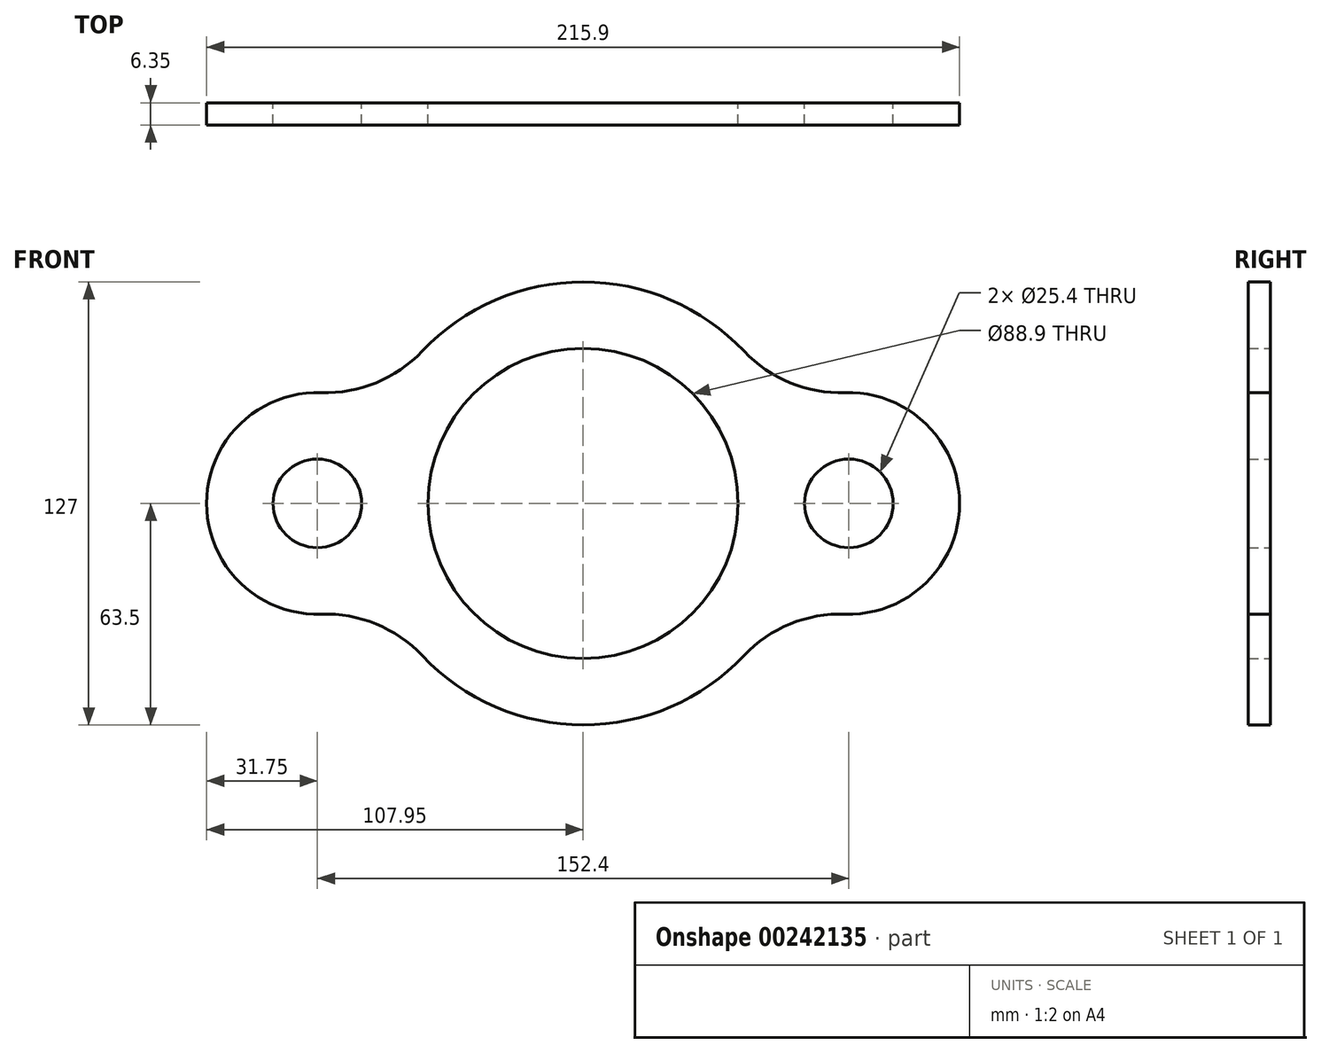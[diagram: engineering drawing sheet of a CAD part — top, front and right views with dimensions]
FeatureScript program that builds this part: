
annotation { "Feature Type Name" : "Feature", "Feature Type Description" : "" }
export const myFeature = defineFeature(function(context is Context, id is Id, definition is map)
    precondition{}
    {
        {
            var Q0;
            Q0=qCreatedBy(makeId("Front.planeOp"),FACE);
            var sketch = newSketch(context, id + "F0", { "sketchPlane" : qUnion([Q0])});
            skCircle(sketch, "E0", {"center": v(0, 0) * mm, "radius": 44.45 * mm});
            skArc(sketch, "E1", {"start": v(75.12, -31.73) * mm, "mid": v(107.95, 0) * mm, "end": v(75.12, 31.73) * mm});
            skArc(sketch, "E2", {"start": v(46.14, 43.63) * mm, "mid": v(0, 63.5) * mm, "end": v(-46.14, 43.63) * mm});
            skCircle(sketch, "E3", {"center": v(76.2, 0) * mm, "radius": 12.7 * mm});
            skArc(sketch, "E4", {"start": v(46.14, 43.63) * mm, "mid": v(59.35, 34.56) * mm, "end": v(75.12, 31.73) * mm});
            skArc(sketch, "E5.MirrorCS", {"start": v(-46.14, 43.63) * mm, "mid": v(-59.35, 34.56) * mm, "end": v(-75.12, 31.73) * mm});
            skArc(sketch, "E6.MirrorCS", {"start": v(-75.12, -31.73) * mm, "mid": v(-107.95, 0) * mm, "end": v(-75.12, 31.73) * mm});
            skArc(sketch, "E7.MirrorCS", {"start": v(46.14, -43.63) * mm, "mid": v(0, -63.5) * mm, "end": v(-46.14, -43.63) * mm});
            skArc(sketch, "E8.MirrorCS", {"start": v(-46.14, -43.63) * mm, "mid": v(-59.35, -34.56) * mm, "end": v(-75.12, -31.73) * mm});
            skArc(sketch, "E9.MirrorCS", {"start": v(46.14, -43.63) * mm, "mid": v(59.35, -34.56) * mm, "end": v(75.12, -31.73) * mm});
            skPoint(sketch, "E10.orphan", {"position": v(-57.94, -25.98) * mm});
            skPoint(sketch, "E11.orphan", {"position": v(57.94, -25.98) * mm});
            skPoint(sketch, "E12.start.orphan", {"position": v(-44.45, 0) * mm});
            skPoint(sketch, "E13.start.orphan", {"position": v(0, -44.45) * mm});
            skCircle(sketch, "E14.MirrorC", {"center": v(-76.2, 0) * mm, "radius": 12.7 * mm});
            skSolve(sketch);
        }
        {
            var Q0;
            Q0=makeQuery(id+"F0.imprint","IMPRINT",FACE,{"disambiguationData":[TD([[makeQuery(id+"F0.imprint","IMPRINT",EDGE,{"derivedFrom":sQuery(id+"F0.wireOp",EDGE,"E0")}),-1.0]])]});
            extrude(context, id + "F1", {"entities" : qUnion([Q0]), "depth" : 6.35 * mm});
        }
    });
